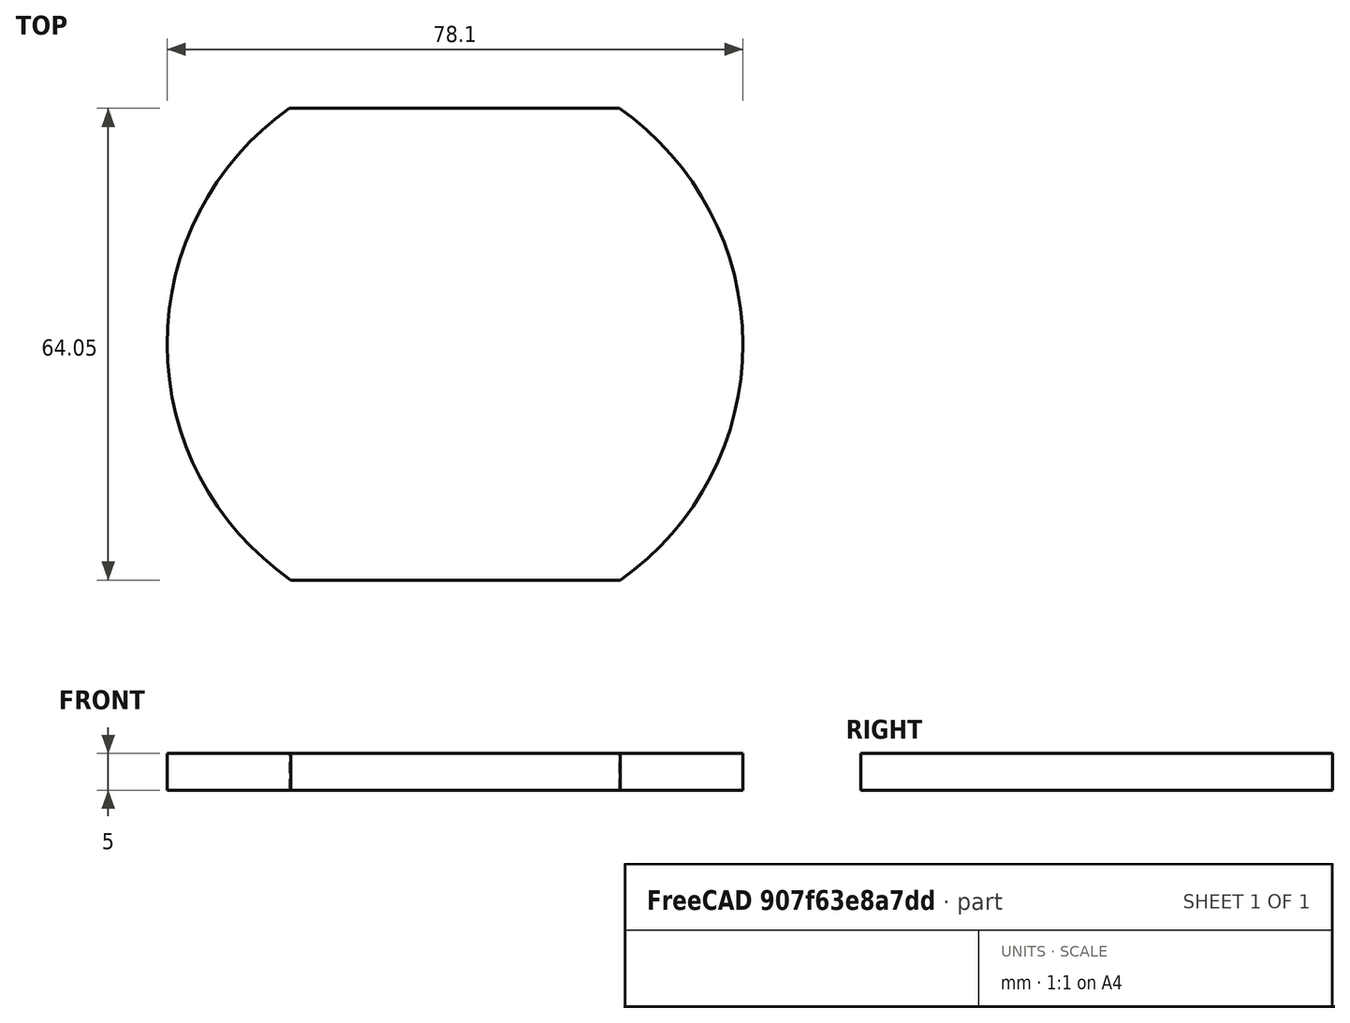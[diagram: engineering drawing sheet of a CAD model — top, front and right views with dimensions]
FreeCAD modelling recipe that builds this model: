
FCSTD DOCUMENT  (FreeCAD 1.0R39319 (Git))
Label: chapa_circle_90mm
License: All rights reserved
LicenseURL: https://en.wikipedia.org/wiki/All_rights_reserved
objects: Sketcher::SketchObject×1, PartDesign::Pad×1, PartDesign::Body×1
note: 6 computed .brp shape members not serialized (recipe doc carries the construction recipe); baked Part::Feature solids carry a one-line shape summary decoded from their .brp

FEATURE [Sketcher::SketchObject] Sketch_1
  ArcFitTolerance = 1e-06
  AttachmentSupport = -> [XY_Plane]
  FullyConstrained = false
  MakeInternals = false
  MapMode = 5
  sketch-geometry (4):
    g0: ArcOfCircle CenterX=-0.00137365 CenterY=6.62952 CenterZ=0 NormalX=0 NormalY=0 NormalZ=1 AngleXU=0 Radius=39.0547 StartAngle=5.32483 EndAngle=7.24741
    g1: LineSegment StartX=22.262 StartY=38.7171 StartZ=0 EndX=-22.4508 EndY=38.7171 EndZ=0
    g2: ArcOfCircle CenterX=0.00220858 CenterY=6.76106 CenterZ=0 NormalX=0 NormalY=0 NormalZ=1 AngleXU=0 Radius=39.0554 StartAngle=2.18328 EndAngle=4.1058
    g3: LineSegment StartX=-22.262 StartY=-25.3268 StartZ=0 EndX=22.4499 EndY=-25.3268 EndZ=0
  constraints (7):
    c: Coincident(g0,g1)
    c: Coincident(g1,g2)
    c: Coincident(g2,g3)
    c: Coincident(g3,g0)
    c: Parallel(g1,g3)
    c: Horizontal(g1)
    c: Distance(g1,g3) = 78
FEATURE [PartDesign::Pad] Pad_1
  Direction = (0,0,1)
  Length = 5
  Length2 = 10
  Profile = -> Sketch_1
  Refine = true
  Suppressed = false
  Type = 0
FEATURE [PartDesign::Body] Body
  AllowCompound = false
  Group = -> [Sketch_1,Pad_1]
  Origin = -> Origin
  Tip = -> Pad_1
